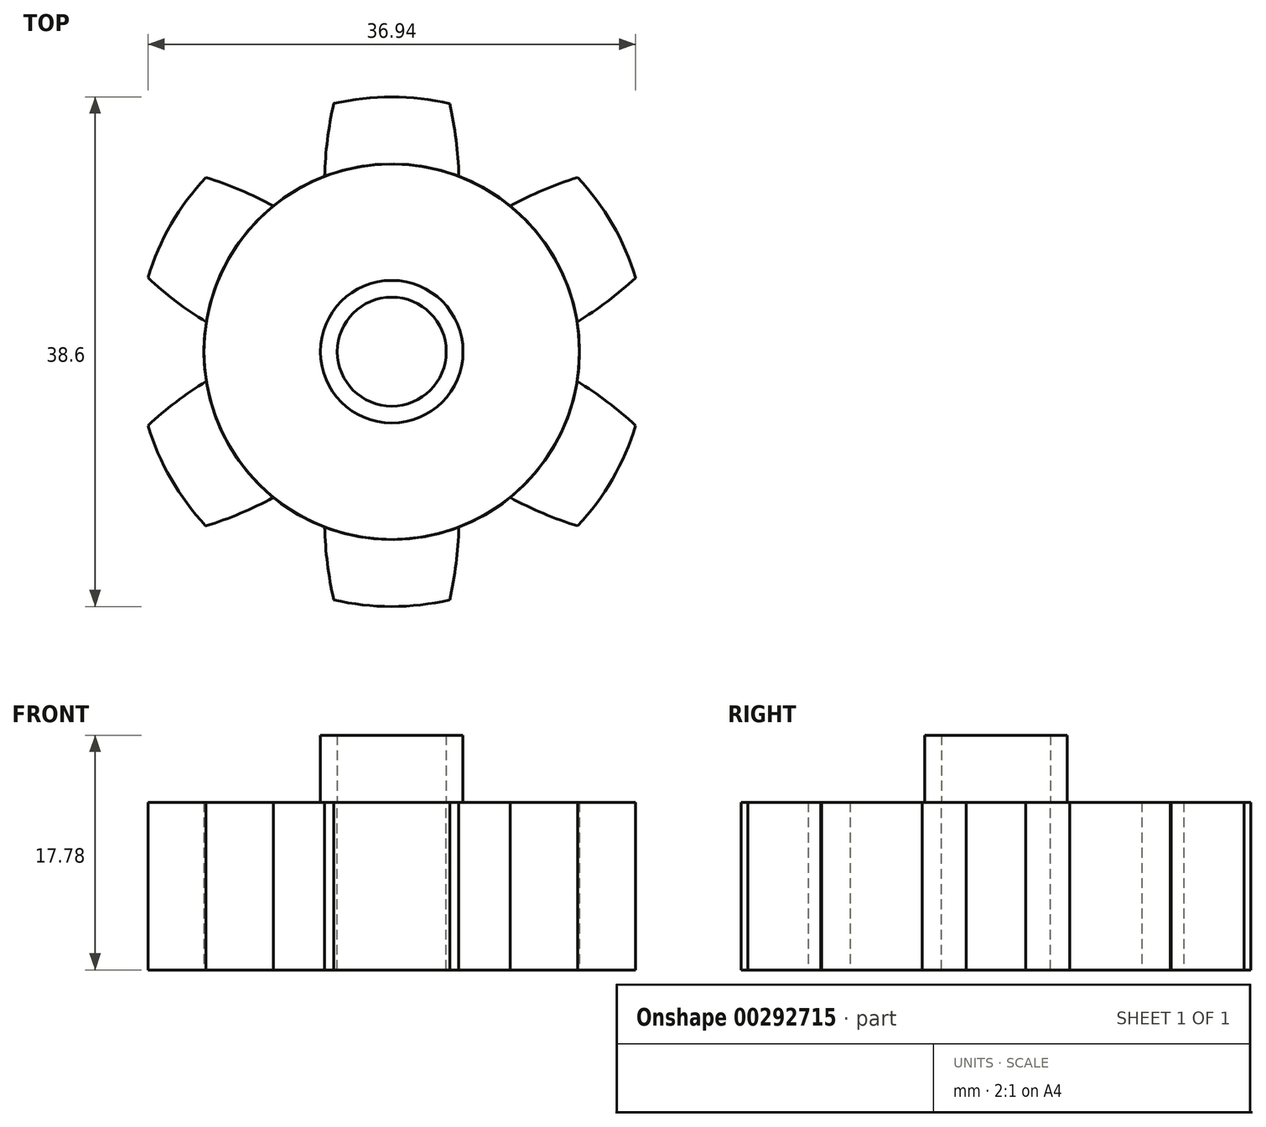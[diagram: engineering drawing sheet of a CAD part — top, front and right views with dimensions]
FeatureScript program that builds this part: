
annotation { "Feature Type Name" : "Feature", "Feature Type Description" : "" }
export const myFeature = defineFeature(function(context is Context, id is Id, definition is map)
    precondition{}
    {
        {
            var Q0;
            Q0=qCreatedBy(makeId("Top.planeOp"),FACE);
            var sketch = newSketch(context, id + "F0", { "sketchPlane" : qUnion([Q0])});
            skCircle(sketch, "E0", {"center": v(0, 0) * mm, "radius": 19.3 * mm});
            skLineSegment(sketch, "E1", {"start": v(0, 0) * mm, "end": v(0, 30.73) * mm});
            skLineSegment(sketch, "E2", {"start": v(0, 19.3) * mm, "end": v(0, 24.38) * mm});
            skArc(sketch, "E3", {"start": v(-2.54, 24.25) * mm, "mid": v(2.05, -24.3) * mm, "end": v(-1.56, 24.33) * mm});
            skCircle(sketch, "E4", {"center": v(0, 0) * mm, "radius": 14.22 * mm});
            skLineSegment(sketch, "E5", {"start": v(0, 14.22) * mm, "end": v(-5.08, 14.22) * mm});
            skLineSegment(sketch, "E6", {"start": v(0, 14.22) * mm, "end": v(5.08, 14.22) * mm});
            skArc(sketch, "E7", {"start": v(-4.4, 18.8) * mm, "mid": v(-4.87, 16.06) * mm, "end": v(-5.08, 13.29) * mm});
            skArc(sketch, "E8", {"start": v(5.08, 13.29) * mm, "mid": v(4.87, 16.06) * mm, "end": v(4.4, 18.8) * mm});
            skArc(sketch, "E9", {"start": v(1.56, 24.33) * mm, "mid": v(-0.5, 24.38) * mm, "end": v(-2.54, 24.25) * mm});
            skArc(sketch, "E10", {"start": v(-1.56, 24.33) * mm, "mid": v(-3.19, 21.68) * mm, "end": v(-4.37, 18.8) * mm});
            skArc(sketch, "E11", {"start": v(4.4, 18.79) * mm, "mid": v(3.17, 21.66) * mm, "end": v(1.56, 24.33) * mm});
            skSolve(sketch);
        }
        {
            var Q0;
            {var subQ0=sQuery(id+"F0.wireOp",EDGE,"E2");Q0=makeQuery(id+"F0.imprint","IMPRINT",FACE,{"disambiguationData":[TD([[makeQuery(id+"F0.imprint","IMPRINT",EDGE,{"derivedFrom":subQ0}),-1.0]])]});}
            var Q1;
            {var subQ0=sQuery(id+"F0.wireOp",EDGE,"E2");Q1=makeQuery(id+"F0.imprint","IMPRINT",FACE,{"disambiguationData":[TD([[makeQuery(id+"F0.imprint","IMPRINT",EDGE,{"derivedFrom":subQ0}),1.0]])]});}
            var Q2;
            {var subQ0=sQuery(id+"F0.wireOp",EDGE,"E4");var subQ3=makeQuery(id+"F0.imprint","INTERSECT",VERTEX,{"derivedFrom":[subQ0,sQuery(id+"F0.wireOp",EDGE,"E7")]});Q2=makeQuery(id+"F0.imprint","IMPRINT",FACE,{"disambiguationData":[TD([[makeQuery(id+"F0.imprint","IMPRINT",EDGE,{"disambiguationData":[TD([[subQ3,-1.0]])],"derivedFrom":subQ0}),1.0]])]});}
            var Q3;
            {var subQ3=sQuery(id+"F0.wireOp",EDGE,"E7");var subQ5=sQuery(id+"F0.wireOp",EDGE,"E5");var subQ7=makeQuery(id+"F0.imprint","INTERSECT",VERTEX,{"derivedFrom":[subQ5,subQ3]});Q3=makeQuery(id+"F0.imprint","IMPRINT",FACE,{"disambiguationData":[TD([[makeQuery(id+"F0.imprint","IMPRINT",EDGE,{"disambiguationData":[TD([[subQ7,1.0]])],"derivedFrom":subQ3}),1.0]])]});}
            var Q4;
            {var subQ3=sQuery(id+"F0.wireOp",EDGE,"E8");var subQ5=sQuery(id+"F0.wireOp",EDGE,"E6");var subQ7=makeQuery(id+"F0.imprint","INTERSECT",VERTEX,{"derivedFrom":[subQ5,subQ3]});Q4=makeQuery(id+"F0.imprint","IMPRINT",FACE,{"disambiguationData":[TD([[makeQuery(id+"F0.imprint","IMPRINT",EDGE,{"disambiguationData":[TD([[subQ7,-1.0]])],"derivedFrom":subQ3}),1.0]])]});}
            var Q5;
            {var subQ1=sQuery(id+"F0.wireOp",EDGE,"E4");var subQ3=sQuery(id+"F0.wireOp",EDGE,"E8");var subQ4=makeQuery(id+"F0.imprint","INTERSECT",VERTEX,{"derivedFrom":[subQ1,subQ3]});Q5=makeQuery(id+"F0.imprint","IMPRINT",FACE,{"disambiguationData":[TD([[makeQuery(id+"F0.imprint","IMPRINT",EDGE,{"disambiguationData":[TD([[subQ4,-1.0]])],"derivedFrom":subQ3}),1.0]])]});}
            var Q6;
            {var subQ1=sQuery(id+"F0.wireOp",EDGE,"E4");var subQ3=sQuery(id+"F0.wireOp",EDGE,"E7");var subQ4=makeQuery(id+"F0.imprint","INTERSECT",VERTEX,{"derivedFrom":[subQ1,subQ3]});Q6=makeQuery(id+"F0.imprint","IMPRINT",FACE,{"disambiguationData":[TD([[makeQuery(id+"F0.imprint","IMPRINT",EDGE,{"disambiguationData":[TD([[subQ4,1.0]])],"derivedFrom":subQ3}),1.0]])]});}
            extrude(context, id + "F1", {"entities" : qUnion([Q0, Q1, Q2, Q3, Q4, Q5, Q6]), "depth" : 12.7 * mm});
        }
        {
            var Q0;
            Q0=makeQuery(id+"F1.opExtrude","SWEPT_BODY",BODY,{"disambiguationData":[OSD([sQuery(id+"F0.wireOp",EDGE,"E3"),sQuery(id+"F0.wireOp",EDGE,"E4"),sQuery(id+"F0.wireOp",EDGE,"E7"),sQuery(id+"F0.wireOp",EDGE,"E8")])]});
            var Q1;
            Q1=makeQuery(id+"F1.opExtrude","SWEPT_FACE",FACE,{"disambiguationData":[OSD([sQuery(id+"F0.wireOp",EDGE,"E4")])]});
            circularPattern(context, id + "F2", {"entities" : qUnion([Q0]), "axis" : qUnion([Q1]), "angle" : 360 * degree, "instanceCount" : 6, "equalSpace" : true});
        }
        {
            var Q0;
            Q0=makeQuery(id+"F1.opExtrude","CAP_FACE",FACE,{"disambiguationData":[OSD([sQuery(id+"F0.wireOp",EDGE,"E0"),sQuery(id+"F0.wireOp",EDGE,"E4"),sQuery(id+"F0.wireOp",EDGE,"E7"),sQuery(id+"F0.wireOp",EDGE,"E8"),sQuery(id+"F0.wireOp",EDGE,"E9"),sQuery(id+"F0.wireOp",EDGE,"E10"),sQuery(id+"F0.wireOp",EDGE,"E11")])],"isStart":false});
            var sketch = newSketch(context, id + "F3", { "sketchPlane" : qUnion([Q0])});
            skCircle(sketch, "E12", {"center": v(0, 0) * mm, "radius": 4.13 * mm});
            skSolve(sketch);
        }
        {
            var Q0;
            Q0 = qSketchRegion(id + "F3", true);
            extrude(context, id + "F4", {"entities" : qUnion([Q0]), "operationType" : NewBodyOperationType.REMOVE, "oppositeDirection" : true, "depth" : 25.4 * mm});
        }
        {
            var Q0;
            Q0=makeQuery(id+"F2.opPattern","COPY",FACE,{"derivedFrom":makeQuery(id+"F1.opExtrude","CAP_FACE",FACE,{"disambiguationData":[OSD([sQuery(id+"F0.wireOp",EDGE,"E0"),sQuery(id+"F0.wireOp",EDGE,"E4"),sQuery(id+"F0.wireOp",EDGE,"E7"),sQuery(id+"F0.wireOp",EDGE,"E8"),sQuery(id+"F0.wireOp",EDGE,"E9"),sQuery(id+"F0.wireOp",EDGE,"E10"),sQuery(id+"F0.wireOp",EDGE,"E11")])],"isStart":false}),"instanceName":"5"});
            var sketch = newSketch(context, id + "F5", { "sketchPlane" : qUnion([Q0])});
            skCircle(sketch, "E13", {"center": v(0, 0) * mm, "radius": 4.13 * mm});
            skCircle(sketch, "E14", {"center": v(0, 0) * mm, "radius": 5.4 * mm});
            skSolve(sketch);
        }
        {
            var Q0;
            Q0 = qSketchRegion(id + "F5", true);
            extrude(context, id + "F6", {"entities" : qUnion([Q0]), "depth" : 5.08 * mm});
        }
    });
